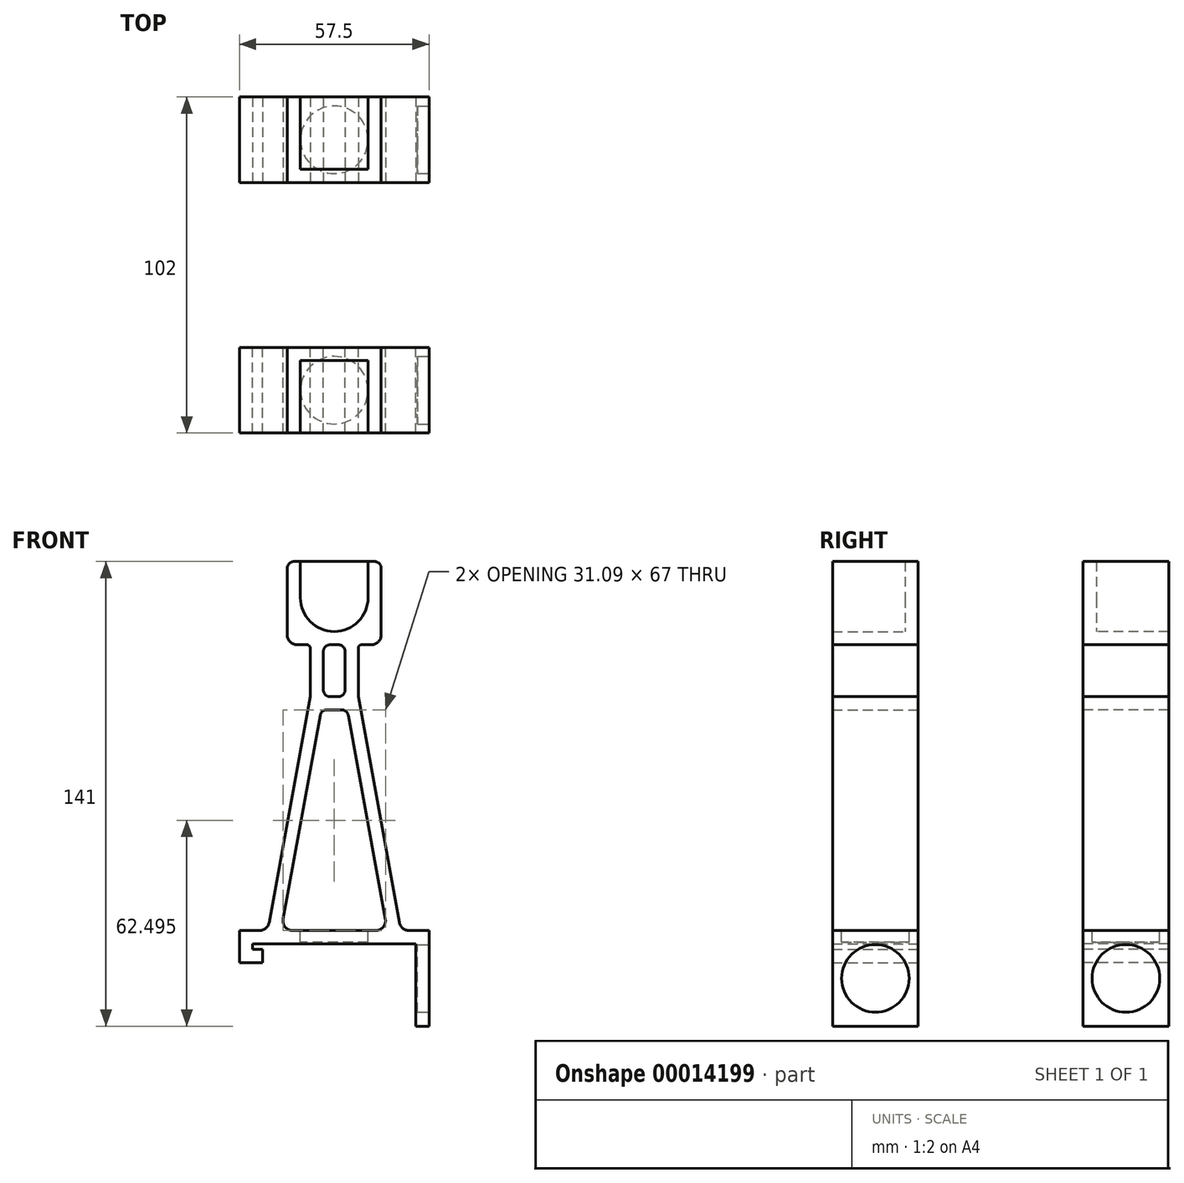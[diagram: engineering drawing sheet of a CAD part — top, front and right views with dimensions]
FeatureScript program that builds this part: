
annotation { "Feature Type Name" : "Feature", "Feature Type Description" : "" }
export const myFeature = defineFeature(function(context is Context, id is Id, definition is map)
    precondition{}
    {
        {
            var Q0;
            Q0=qCreatedBy(makeId("Front.planeOp"),FACE);
            var sketch = newSketch(context, id + "F0", { "sketchPlane" : qUnion([Q0])});
            skLineSegment(sketch, "E0", {"start": v(-28.75, 2.04) * mm, "end": v(-22.71, 2.04) * mm});
            skLineSegment(sketch, "E1", {"start": v(28.75, 2.04) * mm, "end": v(28.75, -26.96) * mm});
            skLineSegment(sketch, "E2", {"start": v(28.75, -26.96) * mm, "end": v(24.75, -26.96) * mm});
            skLineSegment(sketch, "E3", {"start": v(24.75, -26.96) * mm, "end": v(24.75, -1.96) * mm});
            skLineSegment(sketch, "E4", {"start": v(24.75, -1.96) * mm, "end": v(-24.75, -1.96) * mm});
            skLineSegment(sketch, "E5", {"start": v(-24.75, -1.96) * mm, "end": v(-24.75, -3.66) * mm});
            skLineSegment(sketch, "E6", {"start": v(-24.75, -3.66) * mm, "end": v(-21.75, -3.66) * mm});
            skLineSegment(sketch, "E7", {"start": v(-21.75, -3.66) * mm, "end": v(-21.75, -7.66) * mm});
            skLineSegment(sketch, "E8", {"start": v(-21.75, -7.66) * mm, "end": v(-28.75, -7.66) * mm});
            skLineSegment(sketch, "E9", {"start": v(-28.75, -7.66) * mm, "end": v(-28.75, 2.04) * mm});
            skLineSegment(sketch, "E10", {"start": v(-19.76, 4.5) * mm, "end": v(-7.29, 73.04) * mm});
            skLineSegment(sketch, "E11", {"start": v(-1.29, 73.04) * mm, "end": v(1.29, 73.04) * mm});
            skLineSegment(sketch, "E12", {"start": v(7.29, 73.04) * mm, "end": v(19.76, 4.5) * mm});
            skLineSegment(sketch, "E13", {"start": v(-15.5, 5.57) * mm, "end": v(-4.25, 67.4) * mm});
            skLineSegment(sketch, "E14", {"start": v(-2.28, 69.04) * mm, "end": v(2.28, 69.04) * mm});
            skLineSegment(sketch, "E15", {"start": v(4.25, 67.4) * mm, "end": v(15.5, 5.57) * mm});
            skLineSegment(sketch, "E16.trimOffspring", {"start": v(-12.55, 2.04) * mm, "end": v(12.55, 2.04) * mm});
            skLineSegment(sketch, "E17.trimOffspring", {"start": v(22.71, 2.04) * mm, "end": v(28.75, 2.04) * mm});
            skLineSegment(sketch, "E18", {"start": v(-7.29, 73.04) * mm, "end": v(-7.29, 87.79) * mm});
            skLineSegment(sketch, "E19", {"start": v(7.29, 87.79) * mm, "end": v(7.29, 73.04) * mm});
            skLineSegment(sketch, "E20", {"start": v(-3.29, 75.04) * mm, "end": v(-3.29, 86.79) * mm});
            skLineSegment(sketch, "E21", {"start": v(3.29, 86.79) * mm, "end": v(3.29, 75.04) * mm});
            skArc(sketch, "E22", {"start": v(-10.25, 103.04) * mm, "mid": v(0, 92.79) * mm, "end": v(10.25, 103.04) * mm});
            skPoint(sketch, "E22.centerSnap0", {"position": v(0, 73.04) * mm});
            skLineSegment(sketch, "E23", {"start": v(-10.25, 114.04) * mm, "end": v(-10.25, 103.04) * mm});
            skLineSegment(sketch, "E24", {"start": v(10.25, 114.04) * mm, "end": v(10.25, 103.04) * mm});
            skLineSegment(sketch, "E25", {"start": v(-10.25, 114.04) * mm, "end": v(-12.25, 114.04) * mm});
            skLineSegment(sketch, "E26", {"start": v(-14.25, 112.04) * mm, "end": v(-14.25, 91.79) * mm});
            skLineSegment(sketch, "E27", {"start": v(-11.25, 88.79) * mm, "end": v(-8.29, 88.79) * mm});
            skLineSegment(sketch, "E28", {"start": v(14.25, 91.79) * mm, "end": v(14.25, 112.04) * mm});
            skLineSegment(sketch, "E29", {"start": v(12.25, 114.04) * mm, "end": v(10.25, 114.04) * mm});
            skLineSegment(sketch, "E30.trimOffspring", {"start": v(-1.29, 88.79) * mm, "end": v(1.29, 88.79) * mm});
            skLineSegment(sketch, "E31.trimOffspring", {"start": v(8.29, 88.79) * mm, "end": v(11.25, 88.79) * mm});
            skLineSegment(sketch, "E32", {"start": v(-10.25, 114.04) * mm, "end": v(10.25, 114.04) * mm});
            skPoint(sketch, "E33.visualSharp", {"position": v(-14.25, 88.79) * mm});
            skArc(sketch, "E33.filletArc", {"start": v(-14.25, 91.79) * mm, "mid": v(-13.37, 89.66) * mm, "end": v(-11.25, 88.79) * mm});
            skPoint(sketch, "E34.visualSharp", {"position": v(14.25, 88.79) * mm});
            skArc(sketch, "E34.filletArc", {"start": v(11.25, 88.79) * mm, "mid": v(13.37, 89.66) * mm, "end": v(14.25, 91.79) * mm});
            skPoint(sketch, "E35.visualSharp", {"position": v(14.25, 114.04) * mm});
            skArc(sketch, "E35.filletArc", {"start": v(14.25, 112.04) * mm, "mid": v(13.66, 113.45) * mm, "end": v(12.25, 114.04) * mm});
            skPoint(sketch, "E36.visualSharp", {"position": v(-14.25, 114.04) * mm});
            skArc(sketch, "E36.filletArc", {"start": v(-12.25, 114.04) * mm, "mid": v(-13.66, 113.45) * mm, "end": v(-14.25, 112.04) * mm});
            skPoint(sketch, "E37.visualSharp", {"position": v(-7.29, 88.79) * mm});
            skArc(sketch, "E37.filletArc", {"start": v(-7.29, 87.79) * mm, "mid": v(-7.58, 88.5) * mm, "end": v(-8.29, 88.79) * mm});
            skPoint(sketch, "E38.visualSharp", {"position": v(7.29, 88.79) * mm});
            skArc(sketch, "E38.filletArc", {"start": v(8.29, 88.79) * mm, "mid": v(7.58, 88.5) * mm, "end": v(7.29, 87.79) * mm});
            skPoint(sketch, "E39.visualSharp", {"position": v(-3.29, 88.79) * mm});
            skArc(sketch, "E39.filletArc", {"start": v(-1.29, 88.79) * mm, "mid": v(-2.7, 88.2) * mm, "end": v(-3.29, 86.79) * mm});
            skPoint(sketch, "E40.visualSharp", {"position": v(3.29, 88.79) * mm});
            skArc(sketch, "E40.filletArc", {"start": v(3.29, 86.79) * mm, "mid": v(2.7, 88.2) * mm, "end": v(1.29, 88.79) * mm});
            skPoint(sketch, "E41.visualSharp", {"position": v(-3.29, 73.04) * mm});
            skArc(sketch, "E41.filletArc", {"start": v(-3.29, 75.04) * mm, "mid": v(-2.7, 73.62) * mm, "end": v(-1.29, 73.04) * mm});
            skPoint(sketch, "E42.visualSharp", {"position": v(3.29, 73.04) * mm});
            skArc(sketch, "E42.filletArc", {"start": v(1.29, 73.04) * mm, "mid": v(2.7, 73.62) * mm, "end": v(3.29, 75.04) * mm});
            skPoint(sketch, "E43.visualSharp", {"position": v(-3.95, 69.04) * mm});
            skArc(sketch, "E43.filletArc", {"start": v(-2.28, 69.04) * mm, "mid": v(-3.56, 68.57) * mm, "end": v(-4.25, 67.4) * mm});
            skPoint(sketch, "E44.visualSharp", {"position": v(3.95, 69.04) * mm});
            skArc(sketch, "E44.filletArc", {"start": v(4.25, 67.4) * mm, "mid": v(3.56, 68.57) * mm, "end": v(2.28, 69.04) * mm});
            skPoint(sketch, "E45.visualSharp", {"position": v(16.14, 2.04) * mm});
            skArc(sketch, "E45.filletArc", {"start": v(12.55, 2.04) * mm, "mid": v(14.85, 3.11) * mm, "end": v(15.5, 5.57) * mm});
            skPoint(sketch, "E46.visualSharp", {"position": v(-16.14, 2.04) * mm});
            skArc(sketch, "E46.filletArc", {"start": v(-15.5, 5.57) * mm, "mid": v(-14.85, 3.11) * mm, "end": v(-12.55, 2.04) * mm});
            skPoint(sketch, "E47.visualSharp", {"position": v(20.2, 2.04) * mm});
            skArc(sketch, "E47.filletArc", {"start": v(19.76, 4.5) * mm, "mid": v(20.79, 2.73) * mm, "end": v(22.71, 2.04) * mm});
            skPoint(sketch, "E48.visualSharp", {"position": v(-20.2, 2.04) * mm});
            skArc(sketch, "E48.filletArc", {"start": v(-22.71, 2.04) * mm, "mid": v(-20.79, 2.73) * mm, "end": v(-19.76, 4.5) * mm});
            skSolve(sketch);
        }
        {
            var Q0;
            Q0=makeQuery(id+"F0.imprint","IMPRINT",FACE,{"disambiguationData":[TD([[makeQuery(id+"F0.imprint","IMPRINT",EDGE,{"derivedFrom":sQuery(id+"F0.wireOp",EDGE,"E0")}),-1.0]])]});
            extrude(context, id + "F1", {"entities" : qUnion([Q0]), "depth" : 26 * mm});
        }
        {
            var Q0;
            Q0=makeQuery(id+"F1.opExtrude","SWEPT_FACE",FACE,{"disambiguationData":[OSD([sQuery(id+"F0.wireOp",EDGE,"E1")])]});
            var sketch = newSketch(context, id + "F2", { "sketchPlane" : qUnion([Q0])});
            skCircle(sketch, "E49", {"center": v(-13, -12.46) * mm, "radius": 10.25 * mm});
            skPoint(sketch, "E49.centerSnap0", {"position": v(-13, -26.96) * mm});
            skPoint(sketch, "E49.centerSnap1", {"position": v(-26, -12.46) * mm});
            skSolve(sketch);
        }
        {
            var Q0;
            Q0=makeQuery(id+"F2.imprint","IMPRINT",FACE,{"disambiguationData":[TD([[makeQuery(id+"F2.imprint","IMPRINT",EDGE,{"derivedFrom":sQuery(id+"F2.wireOp",EDGE,"E49")}),1.0]])]});
            extrude(context, id + "F3", {"entities" : qUnion([Q0]), "operationType" : NewBodyOperationType.REMOVE, "oppositeDirection" : true, "depth" : 3.5 * mm});
        }
        {
            var Q0;
            Q0=makeQuery(id+"F1.opExtrude","SWEPT_FACE",FACE,{"disambiguationData":[OSD([sQuery(id+"F0.wireOp",EDGE,"E0")])]});
            var sketch = newSketch(context, id + "F4", { "sketchPlane" : qUnion([Q0])});
            skCircle(sketch, "E50", {"center": v(0, -13) * mm, "radius": 10.25 * mm});
            skPoint(sketch, "E50.centerSnap0", {"position": v(-28.75, -13) * mm});
            skSolve(sketch);
        }
        {
            var Q0;
            Q0=makeQuery(id+"F4.imprint","IMPRINT",FACE,{"disambiguationData":[TD([[makeQuery(id+"F4.imprint","IMPRINT",EDGE,{"derivedFrom":sQuery(id+"F4.wireOp",EDGE,"E50")}),1.0]])]});
            extrude(context, id + "F5", {"entities" : qUnion([Q0]), "operationType" : NewBodyOperationType.REMOVE, "oppositeDirection" : true, "depth" : 3.5 * mm});
        }
        {
            var Q0;
            Q0=makeQuery(id+"F0.imprint","IMPRINT",FACE,{"disambiguationData":[TD([[makeQuery(id+"F0.imprint","IMPRINT",EDGE,{"derivedFrom":sQuery(id+"F0.wireOp",EDGE,"E22")}),1.0]])]});
            extrude(context, id + "F6", {"entities" : qUnion([Q0]), "operationType" : NewBodyOperationType.ADD, "depth" : 4 * mm});
        }
        {
            var Q0;
            Q0=qCreatedBy(makeId("Front.planeOp"),FACE);
            cPlane(context, id + "F7", {"entities" : qUnion([Q0]), "cplaneType" : CPlaneType.OFFSET, "offset" : 25 * mm, "oppositeDirection" : true, "width" : 150 * mm, "height" : 150 * mm});
        }
        {
            var Q0;
            Q0=makeQuery(id+"F1.opExtrude","SWEPT_BODY",BODY,{"disambiguationData":[OSD([sQuery(id+"F0.wireOp",EDGE,"E0"),sQuery(id+"F0.wireOp",EDGE,"E1"),sQuery(id+"F0.wireOp",EDGE,"E2"),sQuery(id+"F0.wireOp",EDGE,"E3"),sQuery(id+"F0.wireOp",EDGE,"E4"),sQuery(id+"F0.wireOp",EDGE,"E5"),sQuery(id+"F0.wireOp",EDGE,"E6"),sQuery(id+"F0.wireOp",EDGE,"E7"),sQuery(id+"F0.wireOp",EDGE,"E8"),sQuery(id+"F0.wireOp",EDGE,"E9"),sQuery(id+"F0.wireOp",EDGE,"E10"),sQuery(id+"F0.wireOp",EDGE,"E11"),sQuery(id+"F0.wireOp",EDGE,"E12"),sQuery(id+"F0.wireOp",EDGE,"E13"),sQuery(id+"F0.wireOp",EDGE,"E14"),sQuery(id+"F0.wireOp",EDGE,"E15"),sQuery(id+"F0.wireOp",EDGE,"E16.trimOffspring"),sQuery(id+"F0.wireOp",EDGE,"E17.trimOffspring"),sQuery(id+"F0.wireOp",EDGE,"E18"),sQuery(id+"F0.wireOp",EDGE,"E19"),sQuery(id+"F0.wireOp",EDGE,"E20"),sQuery(id+"F0.wireOp",EDGE,"E21"),sQuery(id+"F0.wireOp",EDGE,"E22"),sQuery(id+"F0.wireOp",EDGE,"E23"),sQuery(id+"F0.wireOp",EDGE,"E24"),sQuery(id+"F0.wireOp",EDGE,"E25"),sQuery(id+"F0.wireOp",EDGE,"E26"),sQuery(id+"F0.wireOp",EDGE,"E27"),sQuery(id+"F0.wireOp",EDGE,"E28"),sQuery(id+"F0.wireOp",EDGE,"E29"),sQuery(id+"F0.wireOp",EDGE,"E30.trimOffspring"),sQuery(id+"F0.wireOp",EDGE,"E31.trimOffspring"),sQuery(id+"F0.wireOp",EDGE,"E33.filletArc"),sQuery(id+"F0.wireOp",EDGE,"E34.filletArc"),sQuery(id+"F0.wireOp",EDGE,"E35.filletArc"),sQuery(id+"F0.wireOp",EDGE,"E36.filletArc"),sQuery(id+"F0.wireOp",EDGE,"E37.filletArc"),sQuery(id+"F0.wireOp",EDGE,"E38.filletArc"),sQuery(id+"F0.wireOp",EDGE,"E39.filletArc"),sQuery(id+"F0.wireOp",EDGE,"E40.filletArc"),sQuery(id+"F0.wireOp",EDGE,"E41.filletArc"),sQuery(id+"F0.wireOp",EDGE,"E42.filletArc"),sQuery(id+"F0.wireOp",EDGE,"E43.filletArc"),sQuery(id+"F0.wireOp",EDGE,"E44.filletArc"),sQuery(id+"F0.wireOp",EDGE,"E45.filletArc"),sQuery(id+"F0.wireOp",EDGE,"E46.filletArc"),sQuery(id+"F0.wireOp",EDGE,"E47.filletArc"),sQuery(id+"F0.wireOp",EDGE,"E48.filletArc")])]});
            var Q1;
            Q1=qCreatedBy(id+"F7.planeOp",FACE);
            mirror(context, id + "F8", {"entities" : qUnion([Q0]), "mirrorPlane" : qUnion([Q1])});
        }
    });
